# Revit family: Blucher_PlumbingFixture_GravityRoofDrain_405.000.075a
name_source: partatom
category: Plumbing Fixtures
revit_build: Autodesk Revit 2017 (Build: 20190508_0315(x64)
units: mm (PartAtom-declared; Revit-internal decimal feet)

## family parameters
Cut with Voids When Loaded = No
Host = Face
OmniClass Number = 23.70.50.21.24
OmniClass Title = Waste Water Drains
Part Type = Normal
Room Calculation Point = No
Round Connector Dimension = Use Diameter
Shared = No

## types (1)
- 75mm
    Assembly Code = D2040200
    AssetType = Fixed
    BIMObjectName = Blucher_PlumbingFixture_GravityRoofDrain_405.000.075
    ClassificationName = Uniclass2015
    ClassificationValue = Pr_65_50_35_37
    Color = Stainless Steel
    D = 75 mm
    Default Elevation = 1219 mm
    DocumentationCertificates = https://www.bimstore.co
    DocumentationInstallationGuide = https://www.bimstore.co
    DocumentationLiterature = https://www.bimstore.co
    DocumentationMaintenance = https://www.bimstore.co
    DocumentationTechnical = https://www.bimstore.co
    DrainMaterial = Blucher_Stainless Steel
    DurationUnit = Years
    ExpectedLife = 50
    Finish = 2B - Pickled
    Grade = AISI 304/EN 1.4301 or AISI 316L/EN 1.4404
    H = 183 mm  [stored 0.600394 ft]
    H1 = 86 mm  [stored 0.282152 ft]
    IfcExportAs = IfcFlowTerminal
    IfcExportType = IfcWasteTerminalTypeEnum.FLOORWASTE
    Keynote = R10
    LowerPartProductCode = 405.000.075
    Manufacturer = BLÜCHER
    ManufacturerName = BLÜCHER
    Material = Available in Stainless Steel AISI 304 & Stainless Steel AISI 316L
    Model = BLÜCHER Gravity Roof Drain
    ModelReference = BLÜCHER Gravity Roof Drain
    NBSDescription = Gravity rainwater outlets
    NBSObjectName = BLÜCHER - Gravity rainwater outlets
    NBSReference = 90-10-20/302
    NominalDepth = 410 mm  [stored 1.34514 ft]
    NominalHeight = 183 mm  [stored 0.600394 ft]
    NominalLength = 410 mm  [stored 1.34514 ft]
    ProductionYear = 2019
    ReferencedStandard = EN1253
    Shape = Rectangular
    Size = 410mm x 410mm x 75mm
    Type Comments = 405.000.075
    TypeName = 405.000.075
    URL = http://www.blucher.com
    UpperPartProductCode = 405.000.000
    WarrantyDurationUnit = Years
    _BSBibleVersion = 15
    _BimSpecGuid = 0
    _CurrentRevision = 1
    _DistributedBy = www.bimstore.co.uk

note: [stored X ft] marks values corroborated as IEEE doubles in the binary element streams (Revit-internal decimal feet)

## geometry (parser evidence)
native form markers: Blend x4, Sweep x10
no freeform markers — native parametric forms only
